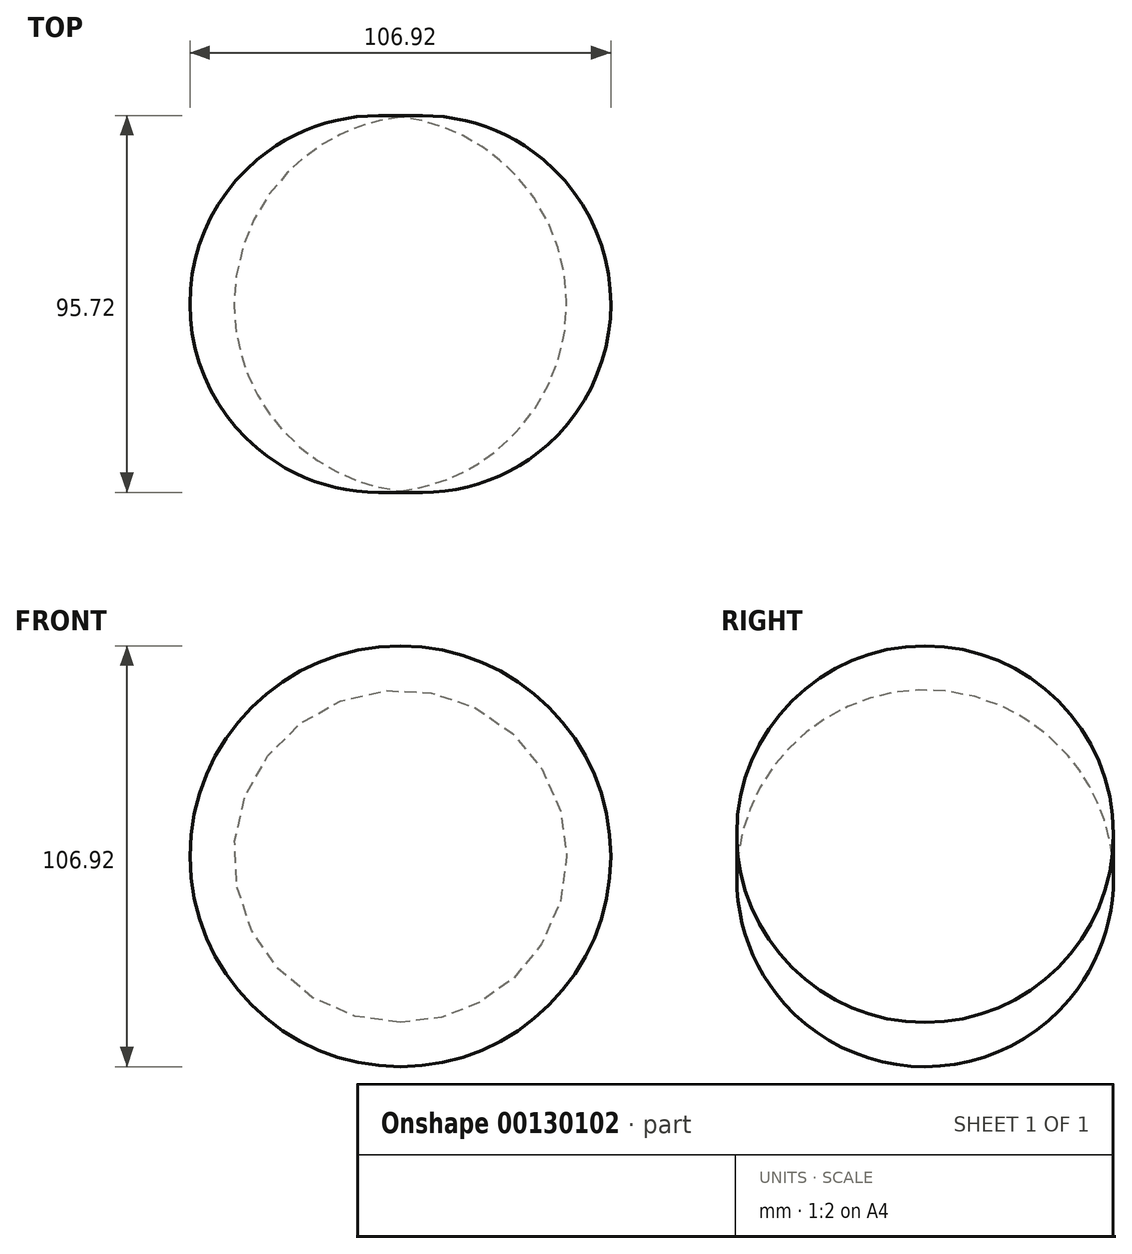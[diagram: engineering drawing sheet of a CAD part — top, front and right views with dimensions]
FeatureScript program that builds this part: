
annotation { "Feature Type Name" : "Feature", "Feature Type Description" : "" }
export const myFeature = defineFeature(function(context is Context, id is Id, definition is map)
    precondition{}
    {
        {
            var Q0;
            Q0=qCreatedBy(makeId("Top.planeOp"),FACE);
            var sketch = newSketch(context, id + "F0", { "sketchPlane" : qUnion([Q0])});
            skLineSegment(sketch, "E0", {"start": v(-32.78, 50.8) * mm, "end": v(-32.78, -44.25) * mm});
            skArc(sketch, "E1", {"start": v(-32.78, -44.25) * mm, "mid": v(20.68, 3.28) * mm, "end": v(-32.78, 50.8) * mm});
            skSolve(sketch);
        }
        {
            var Q0;
            Q0=makeQuery(id+"F0.imprint","IMPRINT",FACE,{"disambiguationData":[TD([[makeQuery(id+"F0.imprint","IMPRINT",EDGE,{"derivedFrom":sQuery(id+"F0.wireOp",EDGE,"E0")}),1.0]])]});
            var sketch = newSketch(context, id + "F1", { "sketchPlane" : qUnion([Q0])});
            skSolve(sketch);
        }
        {
            var Q0;
            Q0 = qSketchRegion(id + "F1", true);
            var Q1;
            Q1=makeQuery(id+"F0.imprint","IMPRINT",FACE,{"disambiguationData":[TD([[makeQuery(id+"F0.imprint","IMPRINT",EDGE,{"derivedFrom":sQuery(id+"F0.wireOp",EDGE,"E0")}),1.0]])]});
            var Q2;
            Q2=sQuery(id+"F0.wireOp",EDGE,"E0");
            revolve(context, id + "F2", {"entities" : qUnion([Q0, Q1]), "axis" : qUnion([Q2]), "revolveType" : RevolveType.FULL});
        }
    });
